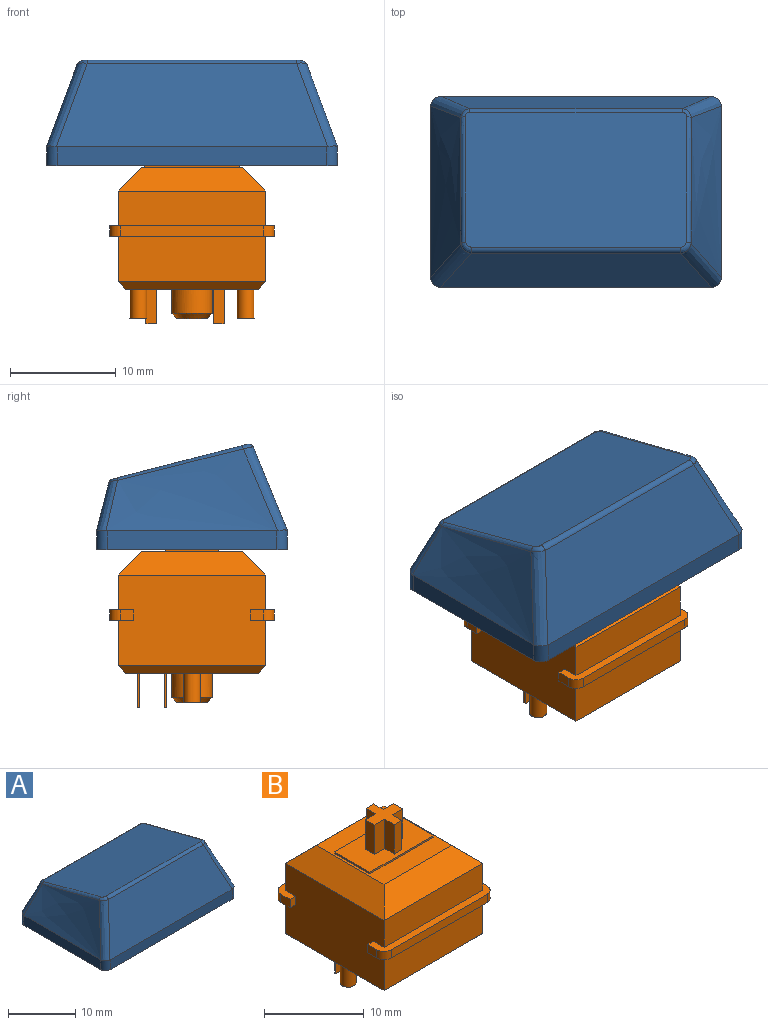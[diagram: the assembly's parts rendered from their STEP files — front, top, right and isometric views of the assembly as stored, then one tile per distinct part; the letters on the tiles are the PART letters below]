
ASSEMBLY  parts=2 mates=1
PART A: 50 faces, bbox 31.9x22.1x14.5 mm
  f0: plane 23.34x14.91mm, normal (0,-0.25,-0.97), area 228.3mm2, adj f31,f32,f33,f34,f47
  f1: plane 16.1x1.8mm, normal (-1,0,0), area 29mm2, adj f5,f10,f11,f17
  f2: plane 25.58x1.8mm, normal (0,-1,0), area 46mm2, adj f5,f9,f11,f13
  f3: plane 16.1x1.8mm, normal (1,0,0), area 29mm2, adj f5,f8,f13,f15
  f4: plane 25.58x1.8mm, normal (0,1,0), area 46mm2, adj f5,f7,f15,f16,f17,f18
  f5: plane 27.58x18.1mm, normal (0,0,-1), area 86.5mm2, adj f1,f2,f3,f4,f11,f13,f15,f17
  f6: plane 21.03x12.77mm, normal (0,0.25,0.97), area 276mm2, adj f19,f20,f21,f22,f23,f24,f25,f26
  f7: plane 25.54x4.53mm, normal (0,0.97,0.25), area 106.7mm2, adj f4,f16,f18,f20
  f8: bspline ~18.1x8.31mm, area 98.6mm2, adj f3,f13,f14,f15,f16,f21
  f9: plane 25.72x7.9mm, normal (0,-0.93,0.38), area 194.5mm2, adj f2,f11,f12,f13,f14,f25
  f10: bspline ~18.1x8.31mm, area 98.6mm2, adj f1,f11,f12,f17,f18,f24
  f11: cylinder r=1mm len=1.87mm, axis (0,0,1), area 2.9mm2, adj f1,f2,f5,f9,f10,f12
  f12: bspline ~11.4x5.55mm, area 13.2mm2, adj f9,f10,f11,f26
  f13: cylinder r=1mm len=1.87mm, axis (0,0,-1), area 2.9mm2, adj f2,f3,f5,f8,f9,f14
  f14: bspline ~11.6x5.63mm, area 13.2mm2, adj f8,f9,f13,f23
  f15: cylinder r=1mm len=1.81mm, axis (0,0,1), area 2.8mm2, adj f3,f4,f5,f8,f16
  f16: bspline ~7.33x5.01mm, area 7.7mm2, adj f4,f7,f8,f15,f19
  f17: cylinder r=1mm len=1.81mm, axis (0,0,-1), area 2.8mm2, adj f1,f4,f5,f10,f18
  f18: bspline ~7.2x4.94mm, area 7.7mm2, adj f4,f7,f10,f17,f22
  f19: bspline ~1.09x0.94mm, area 0.5mm2, adj f6,f16,f20,f21
  f20: cylinder r=0.5mm len=20.15mm, axis (1,0,0), area 10.7mm2, adj f6,f7,f19,f22
  f21: bspline ~15.9x4.31mm, area 7mm2, adj f6,f8,f19,f23
  f22: bspline ~1.16x0.9mm, area 0.5mm2, adj f6,f18,f20,f24
  f23: bspline ~1.22x1.1mm, area 0.8mm2, adj f6,f14,f21,f25
  f24: bspline ~15.86x4.3mm, area 7mm2, adj f6,f10,f22,f26
  f25: cylinder r=0.5mm len=19.85mm, axis (1,0,0), area 14.3mm2, adj f6,f9,f23,f26
  f26: bspline ~1.24x1.04mm, area 0.8mm2, adj f6,f12,f24,f25
  f27: plane 16.18x1.7mm, normal (1,0,0), area 25.3mm2, adj f5,f28,f30,f34
  f28: plane 25.58x1.61mm, normal (0,1,0), area 41.2mm2, adj f5,f27,f29,f33
  f29: plane 16.18x1.7mm, normal (-1,0,0), area 25.3mm2, adj f5,f28,f30,f32
  f30: plane 25.58x1.67mm, normal (0,-1,0), area 42.8mm2, adj f5,f27,f29,f31,f32,f34
  f31: plane 25.4x4.13mm, normal (0,-0.97,-0.25), area 97.5mm2, adj f0,f30,f32,f34
  f32: offset ~20.1x10.31mm, area 90.9mm2, adj f0,f29,f30,f31,f33
  f33: plane 25.62x7.36mm, normal (0,0.93,-0.38), area 180.8mm2, adj f0,f28,f32,f34
  f34: offset ~20.1x10.31mm, area 90.8mm2, adj f0,f27,f30,f31,f33
  f35: plane 7.09x1mm, normal (0,-1,0), area 7.1mm2, adj f36,f46,f48,f49
  f36: plane 7.44x1.35mm, normal (-1,0,0), area 9.8mm2, adj f35,f37,f48,f49
  f37: plane 7.44x1.5mm, normal (0,-1,0), area 11.2mm2, adj f36,f38,f48,f49
  f38: plane 7.77x1.3mm, normal (-1,0,0), area 9.9mm2, adj f37,f39,f48,f49
  f39: plane 7.77x1.5mm, normal (0,1,0), area 11.7mm2, adj f38,f40,f48,f49
  f40: plane 8.12x1.35mm, normal (-1,0,0), area 10.7mm2, adj f39,f41,f48,f49
  f41: plane 8.12x1mm, normal (0,1,0), area 8.1mm2, adj f40,f42,f48,f49
  f42: plane 8.12x1.35mm, normal (1,0,0), area 10.7mm2, adj f41,f43,f48,f49
  f43: plane 7.77x1.5mm, normal (0,1,0), area 11.7mm2, adj f42,f44,f48,f49
  f44: plane 7.77x1.3mm, normal (1,0,0), area 9.9mm2, adj f43,f45,f48,f49
  f45: plane 7.44x1.5mm, normal (0,-1,0), area 11.2mm2, adj f44,f46,f48,f49
  f46: plane 7.44x1.35mm, normal (1,0,0), area 9.8mm2, adj f35,f45,f48,f49
  f47: cylinder r=2.75mm len=6.89mm, axis (0,0,-1), area 119.1mm2, adj f0,f48
  f48: plane 5.5x5.5mm, normal (0,0,-1), area 15.9mm2, adj f35,f36,f37,f38,f39,f40,f41,f42
  f49: plane 4x4mm, normal (0,-0.25,-0.97), area 8.2mm2, adj f35,f36,f37,f38,f39,f40,f41,f42
PART B: 69 faces, bbox 15.6x15.6x18.6 mm
  f0: plane 15.6x2.3mm, normal (0,0,-1), area 14.4mm2, adj f2,f3,f28,f30,f35,f60,f62,f63
  f1: plane 15.6x2.3mm, normal (0,0,-1), area 14.4mm2, adj f28,f30,f33,f34,f36,f59,f61,f64
  f2: plane 1.3x1mm, normal (1,0,0), area 1.3mm2, adj f0,f32,f62,f66
  f3: plane 1.3x1mm, normal (-1,0,0), area 1.3mm2, adj f0,f32,f63,f68
  f4: plane 15.6x2.3mm, normal (0,0,1), area 14.4mm2, adj f28,f30,f31,f33,f34,f36,f61,f64
  f5: plane 14x2.2mm, normal (-0.71,0,0.71), area 36.7mm2, adj f6,f7,f26,f30
  f6: plane 14x2.2mm, normal (0,-0.71,0.71), area 36.7mm2, adj f5,f7,f27,f31
  f7: plane 9.6x9.6mm, normal (0,0,1), area 47.2mm2, adj f5,f6,f8,f9,f10,f11,f26,f27
  f8: plane 5x0.2mm, normal (1,0,0), area 1mm2, adj f7,f9,f11,f12
  f9: plane 9x0.2mm, normal (0,1,0), area 1.8mm2, adj f7,f8,f10,f12
  f10: plane 5x0.2mm, normal (-1,0,0), area 1mm2, adj f7,f9,f11,f12
  f11: plane 9x0.2mm, normal (0,-1,0), area 1.8mm2, adj f7,f8,f10,f12
  f12: plane 9x5mm, normal (0,0,1), area 36.9mm2, adj f8,f9,f10,f11,f13,f14,f15,f16
  f13: plane 3.6x1.35mm, normal (1,0,0), area 4.9mm2, adj f12,f14,f24,f25
  f14: plane 3.6x1.08mm, normal (0,1,0), area 3.9mm2, adj f12,f13,f15,f25
  f15: plane 3.6x1.35mm, normal (-1,0,0), area 4.9mm2, adj f12,f14,f16,f25
  f16: plane 3.6x1.46mm, normal (0,1,0), area 5.3mm2, adj f12,f15,f17,f25
  f17: plane 3.6x1.3mm, normal (-1,0,0), area 4.7mm2, adj f12,f16,f18,f25
  f18: plane 3.6x1.46mm, normal (0,-1,0), area 5.3mm2, adj f12,f17,f19,f25
  f19: plane 3.6x1.35mm, normal (-1,0,0), area 4.9mm2, adj f12,f18,f20,f25
  f20: plane 3.6x1.08mm, normal (0,-1,0), area 3.9mm2, adj f12,f19,f21,f25
  f21: plane 3.6x1.35mm, normal (1,0,0), area 4.9mm2, adj f12,f20,f22,f25
  f22: plane 3.6x1.46mm, normal (0,-1,0), area 5.3mm2, adj f12,f21,f23,f25
  f23: plane 3.6x1.3mm, normal (1,0,0), area 4.7mm2, adj f12,f22,f24,f25
  f24: plane 3.6x1.46mm, normal (0,1,0), area 5.3mm2, adj f12,f13,f23,f25
  f25: plane 4x4mm, normal (0,0,1), area 8.1mm2, adj f13,f14,f15,f16,f17,f18,f19,f20
  f26: plane 14x2.2mm, normal (0,0.71,0.71), area 36.7mm2, adj f5,f7,f27,f29
  f27: plane 14x2.2mm, normal (0.71,0,0.71), area 36.7mm2, adj f6,f7,f26,f28
  f28: plane 14x8.6mm, normal (1,0,0), area 117.4mm2, adj f0,f1,f4,f27,f29,f31,f32,f55
  f29: plane 14x3.3mm, normal (0,1,0), area 46.2mm2, adj f26,f28,f30,f32
  f30: plane 14x8.6mm, normal (-1,0,0), area 117.4mm2, adj f0,f1,f4,f5,f29,f31,f32,f57
  f31: plane 14x3.3mm, normal (0,-1,0), area 46.2mm2, adj f4,f6,f28,f30
  f32: plane 15.6x2.3mm, normal (0,0,1), area 14.4mm2, adj f2,f3,f28,f29,f30,f35,f62,f63
  f33: plane 13.6x1mm, normal (0,-1,0), area 13.6mm2, adj f1,f4,f61,f64
  f34: plane 1.3x1mm, normal (1,0,0), area 1.3mm2, adj f1,f4,f61,f65
  f35: plane 13.6x1mm, normal (0,1,0), area 13.6mm2, adj f0,f32,f62,f63
  f36: plane 1.3x1mm, normal (-1,0,0), area 1.3mm2, adj f1,f4,f64,f67
  f37: plane 2.85x2.85mm, normal (0,0,-1), area 6.4mm2, adj f38
  f38: cone r=1.43mm half-angle=45deg, axis (0,0,1), area 7.4mm2, adj f37,f43
  f39: plane 1x0.2mm, normal (0,0,-1), area 0.2mm2, adj f44,f45,f46,f47
  f40: plane 1x0.2mm, normal (0,0,-1), area 0.2mm2, adj f48,f49,f50,f51
  f41: plane 1.6x1.6mm, normal (0,0,-1), area 2mm2, adj f52
  f42: plane 1.6x1.6mm, normal (0,0,-1), area 2mm2, adj f53
  f43: cylinder r=1.93mm len=3.85mm, axis (0,0,1), area 27.8mm2, adj f38,f54
  f44: plane 3.3x0.2mm, normal (-1,0,0), area 0.7mm2, adj f39,f45,f47,f54
  f45: plane 3.3x1mm, normal (0,1,0), area 3.3mm2, adj f39,f44,f46,f54
  f46: plane 3.3x0.2mm, normal (1,0,0), area 0.7mm2, adj f39,f45,f47,f54
  f47: plane 3.3x1mm, normal (0,-1,0), area 3.3mm2, adj f39,f44,f46,f54
  f48: plane 3.3x0.2mm, normal (-1,0,0), area 0.7mm2, adj f40,f49,f51,f54
  f49: plane 3.3x1mm, normal (0,1,0), area 3.3mm2, adj f40,f48,f50,f54
  f50: plane 3.3x0.2mm, normal (1,0,0), area 0.7mm2, adj f40,f49,f51,f54
  f51: plane 3.3x1mm, normal (0,-1,0), area 3.3mm2, adj f40,f48,f50,f54
  f52: cylinder r=0.8mm len=2.8mm, axis (0,0,1), area 14.1mm2, adj f41,f54
  f53: cylinder r=0.8mm len=2.8mm, axis (0,0,1), area 14.1mm2, adj f42,f54
  f54: plane 12.6x12.6mm, normal (0,0,-1), area 142.7mm2, adj f43,f44,f45,f46,f47,f48,f49,f50
  f55: plane 14x0.7mm, normal (0.71,0,-0.71), area 13.2mm2, adj f28,f54,f56,f58
  f56: plane 14x0.7mm, normal (0,0.71,-0.71), area 13.2mm2, adj f54,f55,f57,f60
  f57: plane 14x0.7mm, normal (-0.71,0,-0.71), area 13.2mm2, adj f30,f54,f56,f58
  f58: plane 14x0.7mm, normal (0,-0.71,-0.71), area 13.2mm2, adj f54,f55,f57,f59
  f59: plane 14x4.3mm, normal (0,-1,0), area 60.2mm2, adj f1,f28,f30,f58
  f60: plane 14x4.3mm, normal (0,1,0), area 60.2mm2, adj f0,f28,f30,f56
  f61: cylinder r=1mm len=1mm, axis (0,0,-1), area 1.6mm2, adj f1,f4,f33,f34
  f62: cylinder r=1mm len=1mm, axis (0,0,1), area 1.6mm2, adj f0,f2,f32,f35
  f63: cylinder r=1mm len=1mm, axis (0,0,-1), area 1.6mm2, adj f0,f3,f32,f35
  f64: cylinder r=1mm len=1mm, axis (0,0,1), area 1.6mm2, adj f1,f4,f33,f36
  f65: plane 1x0.8mm, normal (0,1,0), area 0.8mm2, adj f1,f4,f28,f34
  f66: plane 1x0.8mm, normal (0,-1,0), area 0.8mm2, adj f0,f2,f28,f32
  f67: plane 1x0.8mm, normal (0,1,0), area 0.8mm2, adj f1,f4,f30,f36
  f68: plane 1x0.8mm, normal (0,-1,0), area 0.8mm2, adj f0,f3,f30,f32
PLACE A t=(0,0,11.7)mm
PLACE B at identity fixed
MATE fastened A.f47 <-> B.f38  axis (0,0,-1) through (0,0,11.7)mm
